# Revit family: Univers-IP44-empty-Surface_mounted-CH-en
name_source: partatom
category: Electrical Equipment
units: mm (PartAtom-declared; Revit-internal decimal feet)

## family parameters
Cut with Voids When Loaded = No
Host = Face
Panel Configuration = Two Columns, Circuits Across
Part Type = Panelboard
Room Calculation Point = No
Round Connector Dimension = Use Diameter
Shared = No

## types (1)
- Surface mounted IP44 W800 H1100 D161 0 Modular spacings - FWB73D1
    Default Elevation = 0 mm  [stored 0 ft]
    EF000003 - Mounting method = EV001247 - Surface mounted/recessed mounted
    EF000007 - Colour = EV000202 - White
    EF000008 - Width = 800 mm  [stored 2.62467 ft]
    EF000040 - Height = 1100 mm
    EF000049 - Depth = 161 mm  [stored 0.528215 ft]
    EF000116 - RAL-number = 9010
    EF000118 - With mounting plate = No
    EF000218 - Built-in depth = 161 mm  [stored 0.528215 ft]
    EF000266 - Number of rows = 0
    EF000332 - Built-in height = 1100 mm
    EF000339 - Type of cover = EV000494 - None
    EF000846 - Built-in width = 800 mm  [stored 2.62467 ft]
    EF001062 - EMC-version = No
    EF001088 - Extension possible = No
    EF001131 - Internal depth = 160 mm
    EF001134 - DIN-rail = No
    EF001596 - Material housing = EV000179 - Steel
    EF002950 - Width in number of modular spacings = 0
    EF004462 - Type of closure = EV000154 - Other
    EF005474 - Degree of protection (IP) = EV006418 - IP44
    EF006244 - Transparent cover/door = No
    EF006306 - With lock = No
    EF009212 - Cover model = EV009916 - With notch
    EF015776 - Earthing terminal block = No
    EF015777 - Neutral terminal block = No
    EF015941 - Signal passing door = No
    HG000001 - Number of columns = 0
    HG000002 - With door or cover = No
    HG000003 - Range = Univers
    HG000004 - Manufacturer reference = FWB73D1
    HG000005 - Thickness = 3 mm  [stored 0.00984252 ft]
    HG000006 - Flush mounted = No
    HG000007 - Number of empty columns = 0
    HG000008 - Number of empty rows = 0
    HG000009 - Double swing door = No
    HG000010 - Asymmetric doors = No
    HG000011 - Empty rows from bottom = No
    Manufacturer = Hager
    Model = FWB73D1
    Type Comments = Univers

note: [stored X ft] marks values corroborated as IEEE doubles in the binary element streams (Revit-internal decimal feet)

## geometry (parser evidence)
native form markers: Sweep x11
no freeform markers — native parametric forms only
